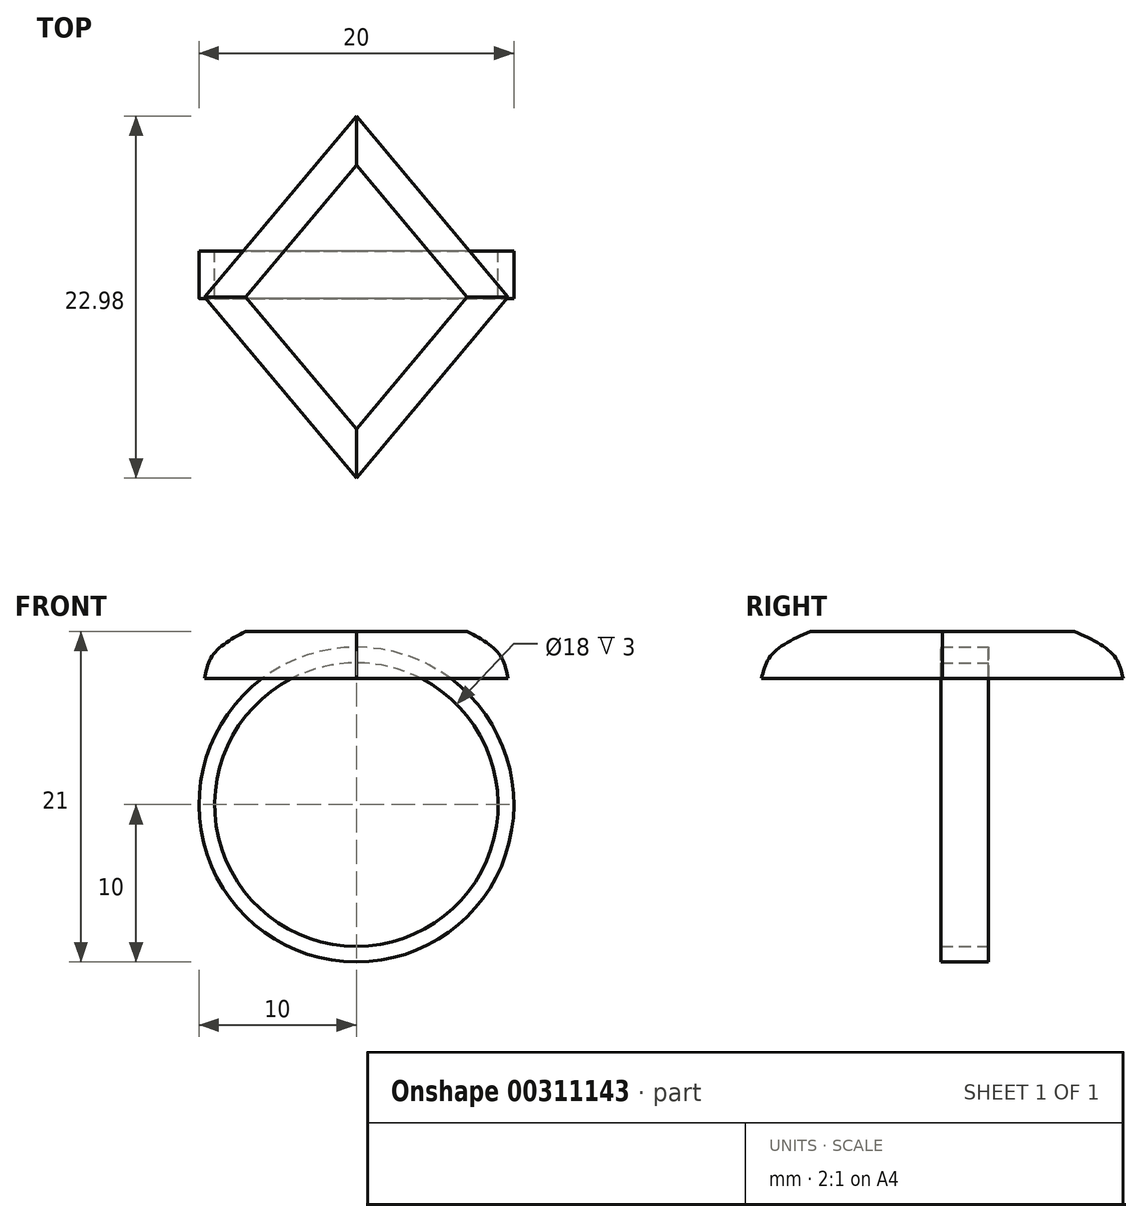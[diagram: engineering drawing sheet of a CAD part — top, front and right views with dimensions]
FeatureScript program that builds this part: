
annotation { "Feature Type Name" : "Feature", "Feature Type Description" : "" }
export const myFeature = defineFeature(function(context is Context, id is Id, definition is map)
    precondition{}
    {
        {
            var Q0;
            Q0=qCreatedBy(makeId("Top.planeOp"),FACE);
            var sketch = newSketch(context, id + "F0", { "sketchPlane" : qUnion([Q0])});
            skLineSegment(sketch, "E0", {"start": v(0, 0) * mm, "end": v(0, 13.4) * mm, "construction": true});
            skPoint(sketch, "E1", {"position": v(0, -6.6) * mm});
            skLineSegment(sketch, "E2", {"start": v(-9.64, 4.89) * mm, "end": v(0, -6.6) * mm});
            skLineSegment(sketch, "E3", {"start": v(9.64, 4.89) * mm, "end": v(0, -6.6) * mm});
            skLineSegment(sketch, "E4", {"start": v(-9.64, 4.89) * mm, "end": v(9.64, 4.89) * mm, "construction": true});
            skLineSegment(sketch, "E5.MirrorCS", {"start": v(-9.64, 4.89) * mm, "end": v(0, 16.38) * mm});
            skLineSegment(sketch, "E6.MirrorCS", {"start": v(9.64, 4.89) * mm, "end": v(0, 16.38) * mm});
            skSolve(sketch);
        }
        {
            var Q0;
            Q0=qCreatedBy(makeId("Top.planeOp"),FACE);
            cPlane(context, id + "F1", {"entities" : qUnion([Q0]), "cplaneType" : CPlaneType.OFFSET, "offset" : 1.5 * mm, "width" : 150 * mm, "height" : 150 * mm});
        }
        {
            var Q0;
            Q0=qCreatedBy(makeId("Top.planeOp"),FACE);
            cPlane(context, id + "F2", {"entities" : qUnion([Q0]), "cplaneType" : CPlaneType.OFFSET, "offset" : 3 * mm, "width" : 150 * mm, "height" : 150 * mm});
        }
        {
            var Q0;
            Q0=qCreatedBy(id+"F2.planeOp",FACE);
            var sketch = newSketch(context, id + "F3", { "sketchPlane" : qUnion([Q0])});
            skLineSegment(sketch, "E7.0", {"start": v(0, -3.5) * mm, "end": v(7.03, 4.89) * mm});
            skLineSegment(sketch, "E7.1", {"start": v(-7.03, 4.89) * mm, "end": v(0, -3.5) * mm});
            skLineSegment(sketch, "E7.2", {"start": v(0, 13.27) * mm, "end": v(-7.03, 4.89) * mm});
            skLineSegment(sketch, "E7.3", {"start": v(7.03, 4.89) * mm, "end": v(0, 13.27) * mm});
            skSolve(sketch);
        }
        {
            var Q0;
            Q0=qCreatedBy(id+"F1.planeOp",FACE);
            var sketch = newSketch(context, id + "F4", { "sketchPlane" : qUnion([Q0])});
            skPoint(sketch, "E8", {"position": v(0, 24.6) * mm});
            skLineSegment(sketch, "E9.0", {"start": v(0, -5.98) * mm, "end": v(9.12, 4.89) * mm});
            skLineSegment(sketch, "E9.1", {"start": v(-9.12, 4.89) * mm, "end": v(0, -5.98) * mm});
            skLineSegment(sketch, "E9.2", {"start": v(0, 15.75) * mm, "end": v(-9.12, 4.89) * mm});
            skLineSegment(sketch, "E9.3", {"start": v(9.12, 4.89) * mm, "end": v(0, 15.75) * mm});
            skSolve(sketch);
        }
        {
            var Q0;
            Q0=qCreatedBy(makeId("Front.planeOp"),FACE);
            cPlane(context, id + "F5", {"entities" : qUnion([Q0]), "cplaneType" : CPlaneType.OFFSET, "offset" : 7.8 * mm, "oppositeDirection" : true, "width" : 152.4 * mm, "height" : 152.4 * mm});
        }
        {
            var Q0;
            Q0=qCreatedBy(id+"F5.planeOp",FACE);
            var sketch = newSketch(context, id + "F6", { "sketchPlane" : qUnion([Q0])});
            skCircle(sketch, "E10", {"center": v(0, -8) * mm, "radius": 9 * mm});
            skPoint(sketch, "E11", {"position": v(0, -17) * mm});
            skPoint(sketch, "E12", {"position": v(0, 1) * mm});
            skCircle(sketch, "E13", {"center": v(0, -8) * mm, "radius": 10 * mm});
            skSolve(sketch);
        }
        {
            var Q0;
            Q0=makeQuery(id+"F0.imprint","IMPRINT",FACE,{"disambiguationData":[TD([[makeQuery(id+"F0.imprint","IMPRINT",EDGE,{"derivedFrom":sQuery(id+"F0.wireOp",EDGE,"E2")}),1.0]])]});
            var Q1;
            Q1=makeQuery(id+"F4.imprint","IMPRINT",FACE,{"disambiguationData":[TD([[makeQuery(id+"F4.imprint","IMPRINT",EDGE,{"derivedFrom":sQuery(id+"F4.wireOp",EDGE,"E9.0")}),1.0]])]});
            var Q2;
            Q2=makeQuery(id+"F3.imprint","IMPRINT",FACE,{"disambiguationData":[TD([[makeQuery(id+"F3.imprint","IMPRINT",EDGE,{"derivedFrom":sQuery(id+"F3.wireOp",EDGE,"E7.0")}),1.0]])]});
            loft(context, id + "F7", {"sheetProfilesArray" : [{ "sheetProfileEntities" : qUnion([Q0]) }, { "sheetProfileEntities" : qUnion([Q1]) }, { "sheetProfileEntities" : qUnion([Q2]) }]});
        }
        {
            var Q0;
            Q0=makeQuery(id+"F6.imprint","IMPRINT",FACE,{"disambiguationData":[TD([[makeQuery(id+"F6.imprint","IMPRINT",EDGE,{"derivedFrom":sQuery(id+"F6.wireOp",EDGE,"E10")}),-1.0]])]});
            extrude(context, id + "F8", {"entities" : qUnion([Q0]), "depth" : 3 * mm});
        }
    });
